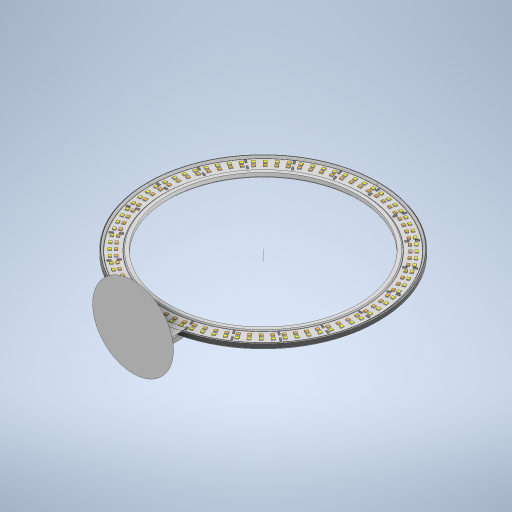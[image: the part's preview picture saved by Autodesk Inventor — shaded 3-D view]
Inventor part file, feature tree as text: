
AUTODESK INVENTOR PART (.ipt)
format: ipt  version: 2024.1 (Build 281209000, 209)  size: 3,019,776 bytes
history: native  units: mm
features: sketch x12, extrude x12, other x9, projected_geometry x9, chamfer x5, pattern_circular x3, fillet x3
ambient origin geometry x8: Origin, YZ Plane, XZ Plane, XY Plane, X Axis, Y Axis, Z Axis, Center Point
bodies: Solid7 (feature_tree), Solid8 (feature_tree), Solid9 (feature_tree)
feature tree (53):
  other  "led-ring"
  sketch  "Sketch1"  dims[d0=221.0mm d1=15.0mm]
  extrude  "Extrusion1"  Depth=15.0mm
  extrude  "Extrusion2"  Depth=2.8mm
  other  "Work Axis1"
  pattern_circular  "Circular Pattern1"  Count=80 Angle=360.0deg
  extrude  "Extrusion3"  Depth=1.44mm
  pattern_circular  "Circular Pattern2"  [2 undecoded]
  extrude  "Extrusion4"  Depth=3.0mm TaperAngle=360.0deg
  chamfer  "Chamfer3"  Distance=5.0mm
  extrude  "Extrusion5"  Depth=3.0mm
  extrude  "Extrusion6"  Depth=3.0mm TaperAngle=0.0deg
  extrude  "Extrusion12"  Depth=3.0mm
  chamfer  "Chamfer4"  Distance=3.0mm
  chamfer  "Chamfer5"  Distance=2.0mm
  pattern_circular  "Circular Pattern3"  [2 undecoded]
  extrude  "Extrusion7"  Depth=3.0mm TaperAngle=0.0deg
  extrude  "Extrusion8"  Depth=3.0mm
  extrude  "Extrusion9"  Depth=3.0mm
  fillet  "Fillet2"  Radius=15.0mm
  fillet  "Fillet3"  Radius=4.0mm
  extrude  "Extrusion10"  Depth=3.0mm TaperAngle=0.0deg
  fillet  "Fillet4"  Radius=10.0mm
  extrude  "Extrusion11"  Depth=3.0mm
  chamfer  "Chamfer6"  Distance=15.0mm
  chamfer  "Chamfer7"  Distance=90.0mm
  sketch  "Sketch2"  dims[d2=1.06mm d3=0.0mm d4=2.8mm]
  projected_geometry  "Projected Loop1"
  sketch  "Sketch3"  dims[d5=3.2mm]
  projected_geometry  "Projected Loop2"
  sketch  "Sketch5"  dims[d6=2.8mm]
  other  "inside-ring-mount"
  sketch  "Sketch6"  dims[d7=3.2mm]
  projected_geometry  "Projected Loop3"
  sketch  "Sketch7"  dims[d8=2.22mm]
  sketch  "Sketch8"  dims[d9=0.9mm d10=0.0mm d11=800.0mm d12=360.0deg]
  sketch  "Sketch9"  dims[d14=1.6mm d15=1.44mm]
  projected_geometry  "Projected Loop4"
  sketch  "Sketch10"  dims[d16=3.6mm]
  other  "RING-STAND"
  projected_geometry  "Projected Loop6"
  sketch  "Sketch12"  dims[d17=3.6mm]
  projected_geometry  "Projected Loop7"
  other  "foot"
  sketch  "Sketch13"  dims[d18=1.53mm]
  projected_geometry  "Projected Loop8"
  other  "outside-ring-mount"
  sketch  "Sketch15"  dims[d19=1.53mm d20=0.7mm d21=0.0mm d22=200.0mm d23=360.0deg d25=5.0mm d26=0.3mm d27=2.1mm d28=0.0mm d29=3.0mm d30=3.0mm d31=2.0mm d32=0.0mm d33=0.4mm d34=5.0mm d35=0.0mm d42=30.0mm d43=30.0mm d44=15.0mm d45=4.0mm d46=9.0mm d47=0.0mm d48=0.0mm d49=2.25mm d50=0.0mm d51=10.0mm d52=0.0mm d55=80.0mm d56=15.0mm d57=90.0mm d58=5.0mm d59=0.0mm d60=20.0mm d61=5.0mm d62=0.0mm d63=1.0mm d64=2.0mm d65=45.0deg d66=3.0mm d67=2.0mm d68=0.0mm d69=2.0mm d70=2.0mm d71=45.0deg d72=0.5mm d73=2.0mm d74=45.0deg d75=40.0mm d76=360.0deg d78=2.0mm d79=2.0mm d80=45.0deg d81=2.0mm d82=2.0mm d83=45.0deg]
  projected_geometry  "Projected Loop9"
  projected_geometry  "Projected Loop10"
  other  "Pattern of outside-ring-mount:1"
  other  "Pattern of outside-ring-mount:2"
  other  "Pattern of outside-ring-mount:3"
note: 4 required parameter values undecoded (feature->parameter linkage not recoverable at this tier; creation-order binding heuristic only, values carry confidence <= 0.55)
